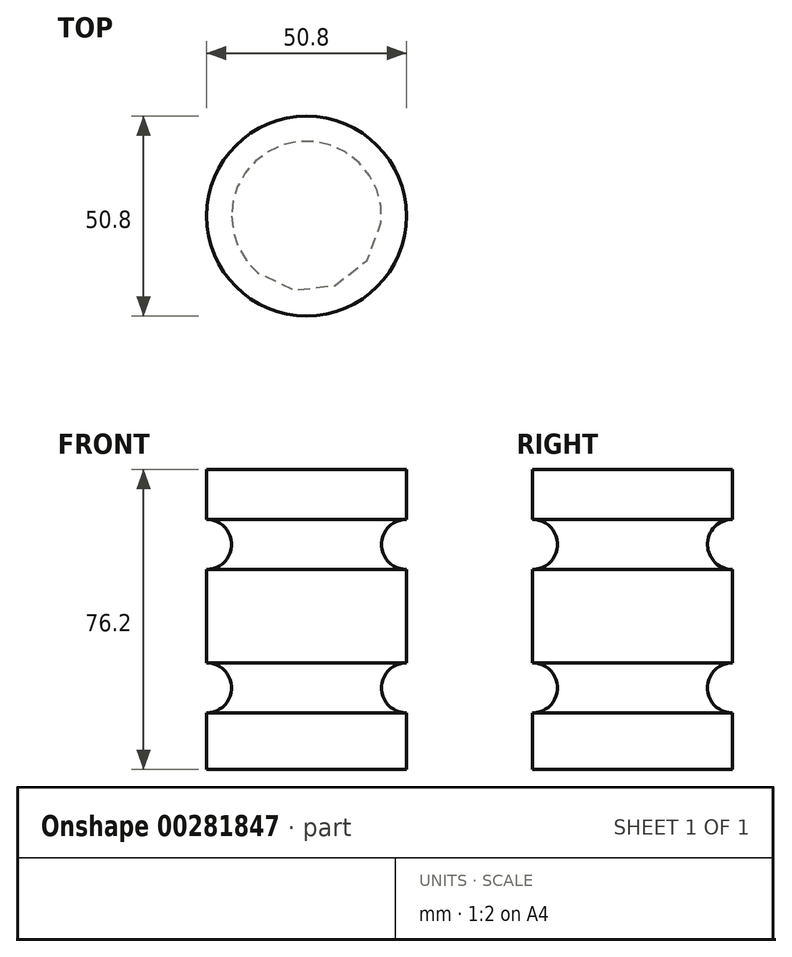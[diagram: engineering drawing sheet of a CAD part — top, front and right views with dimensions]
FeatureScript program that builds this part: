
annotation { "Feature Type Name" : "Feature", "Feature Type Description" : "" }
export const myFeature = defineFeature(function(context is Context, id is Id, definition is map)
    precondition{}
    {
        {
            var Q0;
            Q0=qCreatedBy(makeId("Front.planeOp"),FACE);
            var sketch = newSketch(context, id + "F0", { "sketchPlane" : qUnion([Q0])});
            skLineSegment(sketch, "E0.bottom", {"start": v(0, 0) * mm, "end": v(-25.4, 0) * mm});
            skLineSegment(sketch, "E0.top", {"start": v(0, 76.2) * mm, "end": v(-25.4, 76.2) * mm});
            skLineSegment(sketch, "E0.left", {"start": v(0, 0) * mm, "end": v(0, 76.2) * mm});
            skLineSegment(sketch, "E0.right", {"start": v(-25.4, 0) * mm, "end": v(-25.4, 76.2) * mm});
            skCircle(sketch, "E1", {"center": v(0, 57.17) * mm, "radius": 6.35 * mm});
            skCircle(sketch, "E2", {"center": v(0, 20.74) * mm, "radius": 6.35 * mm});
            skSolve(sketch);
        }
        {
            var Q0;
            {var subQ5=sQuery(id+"F0.wireOp",EDGE,"E0.bottom");Q0=makeQuery(id+"F0.imprint","IMPRINT",FACE,{"disambiguationData":[TD([[makeQuery(id+"F0.imprint","IMPRINT",EDGE,{"derivedFrom":subQ5}),-1.0]])]});}
            var Q1;
            Q1=sQuery(id+"F0.wireOp",EDGE,"E0.right");
            revolve(context, id + "F1", {"entities" : qUnion([Q0]), "axis" : qUnion([Q1]), "revolveType" : RevolveType.FULL});
        }
    });
